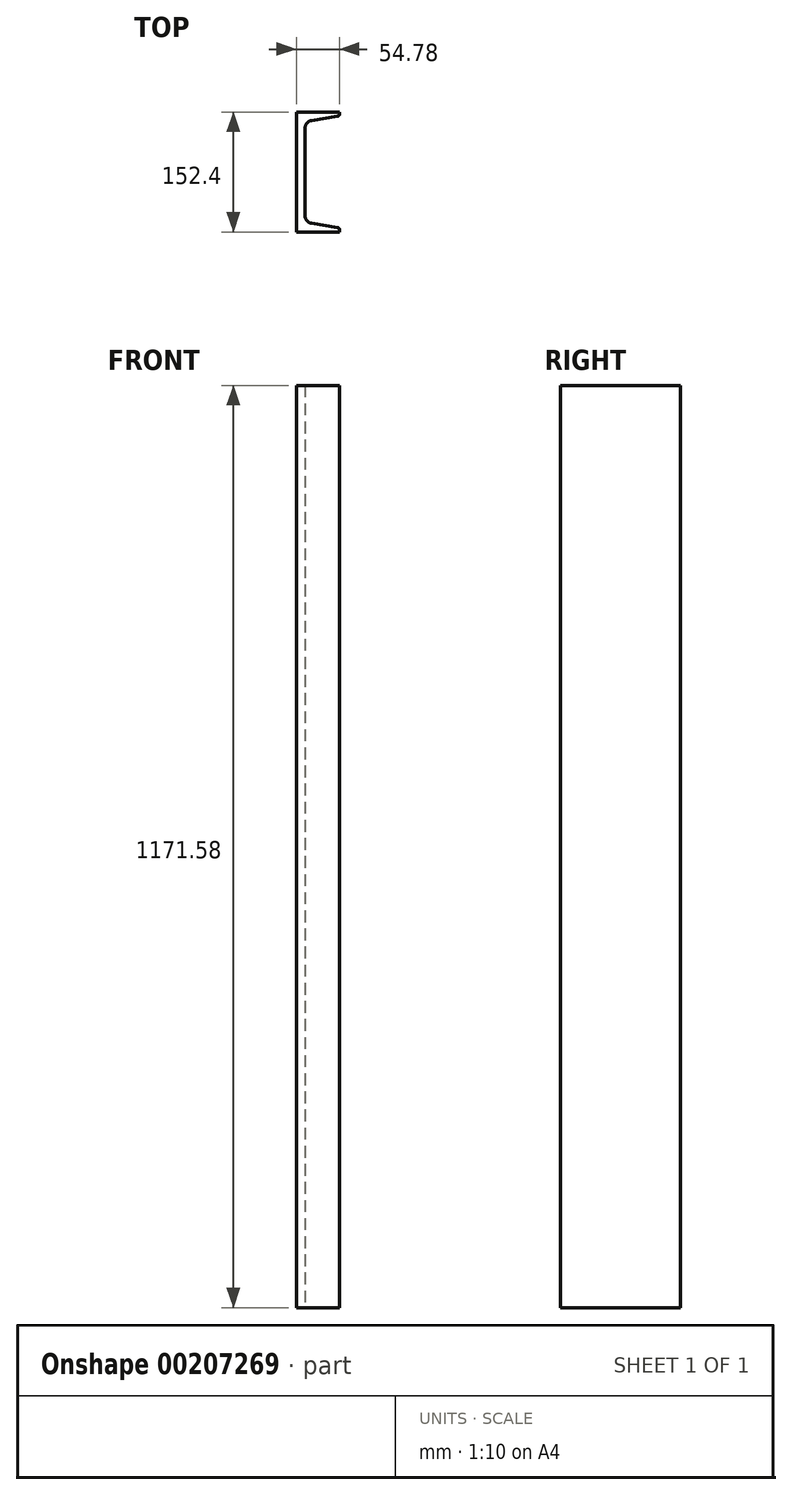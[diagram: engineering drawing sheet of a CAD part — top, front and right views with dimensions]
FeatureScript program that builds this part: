
annotation { "Feature Type Name" : "Feature", "Feature Type Description" : "" }
export const myFeature = defineFeature(function(context is Context, id is Id, definition is map)
    precondition{}
    {
        {
            var Q0;
            Q0=qCreatedBy(makeId("Top.planeOp"),FACE);
            var sketch = newSketch(context, id + "F0", { "sketchPlane" : qUnion([Q0])});
            skLineSegment(sketch, "E0", {"start": v(-27.4, -76.2) * mm, "end": v(-27.4, 76.2) * mm});
            skLineSegment(sketch, "E1", {"start": v(-16.3, -55.87) * mm, "end": v(-16.3, 55.87) * mm});
            skArc(sketch, "E2", {"start": v(27.4, -73.2) * mm, "mid": v(26.77, -71.51) * mm, "end": v(25.2, -70.63) * mm});
            skLineSegment(sketch, "E3", {"start": v(25.2, -70.63) * mm, "end": v(-8.27, -65.28) * mm});
            skLineSegment(sketch, "E4", {"start": v(-27.4, -76.2) * mm, "end": v(27.4, -76.2) * mm});
            skLineSegment(sketch, "E5", {"start": v(27.4, -76.2) * mm, "end": v(27.4, -73.2) * mm});
            skArc(sketch, "E6", {"start": v(-16.3, -55.87) * mm, "mid": v(-14.02, -62.05) * mm, "end": v(-8.27, -65.28) * mm});
            skArc(sketch, "E7", {"start": v(25.2, 70.63) * mm, "mid": v(26.77, 71.51) * mm, "end": v(27.4, 73.2) * mm});
            skLineSegment(sketch, "E8", {"start": v(25.2, 70.63) * mm, "end": v(-8.27, 65.28) * mm});
            skArc(sketch, "E9", {"start": v(-8.27, 65.28) * mm, "mid": v(-14.02, 62.05) * mm, "end": v(-16.3, 55.87) * mm});
            skLineSegment(sketch, "E10", {"start": v(-27.4, 76.2) * mm, "end": v(27.4, 76.2) * mm});
            skLineSegment(sketch, "E11", {"start": v(27.4, 76.2) * mm, "end": v(27.4, 73.2) * mm});
            skSolve(sketch);
        }
        {
            var Q0;
            Q0 = qSketchRegion(id + "F0", true);
            extrude(context, id + "F1", {"entities" : qUnion([Q0]), "depth" : 1171.58 * mm});
        }
    });
